# Revit family: С_Eng
name_source: partatom
category: Mechanical Equipment
units: mm (PartAtom-declared; Revit-internal decimal feet)

## family parameters
Always vertical = Yes
Classification = None
Cut with Voids When Loaded = No
Part Type = Normal
Room Calculation Point = No
Round Connector Dimension = Use Diameter
Shared = No
Work Plane-Based = No

## types (6) — shared parameters
00_20_Manufacturer = Vents
00_20_Name = Axial fan
Amperage = 0 A
Casing Material = Plastic, opaque, white
Grid Material = Mesh, kapron
Load Classification = HVAC
Maintenance zone material = <By Category>
Manufacturer = Vents
Number of Fase = 1
URL = https://ventilation-system.com
Voltage = 230 V
zero-valued in all types: Default Elevation

## per-type parameters (varying)
| type | Apparent Load | B | D | Diameter | Dy | Frequency | H | Height | L | L1 | L2 | Length | Maximum Air Flow | Power | Sound pressure level at 3 m distance | Weight | Width |
| 150 C | 30 W | 205 mm  [stored 0.672572 ft] | 150 mm  [stored 0.492126 ft] | 150 mm  [stored 0.492126 ft] | 145 mm  [stored 0.475722 ft] | 50 Hz | 205 mm  [stored 0.672572 ft] | 205 mm  [stored 0.672572 ft] | 132 mm  [stored 0.433071 ft] | 14 mm  [stored 0.0459318 ft] | 118 mm | 132 mm  [stored 0.433071 ft] | 292.0 m³/h | 24 W | 38 dBA | 1.13 kg | 205 mm  [stored 0.672572 ft] |
| 100 C | 21 W | 150 mm  [stored 0.492126 ft] | 100 mm  [stored 0.328084 ft] | 100 mm  [stored 0.328084 ft] | 95 mm | 50 Hz | 150 mm  [stored 0.492126 ft] | 150 mm  [stored 0.492126 ft] | 108 mm  [stored 0.354331 ft] | 12 mm  [stored 0.0393701 ft] | 96 mm  [stored 0.314961 ft] | 108 mm  [stored 0.354331 ft] | 95.0 m³/h | 14 W | 34 dBA | 0.58 kg | 150 mm  [stored 0.492126 ft] |
| 125 C | 23 W | 176 mm  [stored 0.577428 ft] | 125 mm  [stored 0.410105 ft] | 125 mm  [stored 0.410105 ft] | 120 mm  [stored 0.393701 ft] | 50 Hz | 176 mm  [stored 0.577428 ft] | 176 mm  [stored 0.577428 ft] | 114 mm  [stored 0.374016 ft] | 13 mm  [stored 0.0426509 ft] | 101 mm  [stored 0.331365 ft] | 114 mm  [stored 0.374016 ft] | 180.0 m³/h | 16 W | 35 dBA | 0.75 kg | 176 mm  [stored 0.577428 ft] |
| 100 C (220 В/60 Hz) | 21 W | 150 mm  [stored 0.492126 ft] | 100 mm  [stored 0.328084 ft] | 100 mm  [stored 0.328084 ft] | 95 mm | 60 Hz | 150 mm  [stored 0.492126 ft] | 150 mm  [stored 0.492126 ft] | 108 mm  [stored 0.354331 ft] | 12 mm  [stored 0.0393701 ft] | 96 mm  [stored 0.314961 ft] | 108 mm  [stored 0.354331 ft] | 95.0 m³/h | 14 W | 34 dBA | 0.58 kg | 150 mm  [stored 0.492126 ft] |
| 125 C (220 В/60 Hz) | 23 W | 176 mm  [stored 0.577428 ft] | 125 mm  [stored 0.410105 ft] | 125 mm  [stored 0.410105 ft] | 120 mm  [stored 0.393701 ft] | 60 Hz | 176 mm  [stored 0.577428 ft] | 176 mm  [stored 0.577428 ft] | 114 mm  [stored 0.374016 ft] | 13 mm  [stored 0.0426509 ft] | 101 mm  [stored 0.331365 ft] | 114 mm  [stored 0.374016 ft] | 180.0 m³/h | 16 W | 35 dBA | 0.75 kg | 176 mm  [stored 0.577428 ft] |
| 150 C (220 В/60 Hz) | 30 W | 205 mm  [stored 0.672572 ft] | 150 mm  [stored 0.492126 ft] | 150 mm  [stored 0.492126 ft] | 145 mm  [stored 0.475722 ft] | 60 Hz | 205 mm  [stored 0.672572 ft] | 205 mm  [stored 0.672572 ft] | 132 mm  [stored 0.433071 ft] | 14 mm  [stored 0.0459318 ft] | 118 mm | 132 mm  [stored 0.433071 ft] | 292.0 m³/h | 24 W | 38 dBA | 1.13 kg | 205 mm  [stored 0.672572 ft] |

note: column(s) folded — value = type name in every type: 00_20_Type

note: [stored X ft] marks values corroborated as IEEE doubles in the binary element streams (Revit-internal decimal feet)
